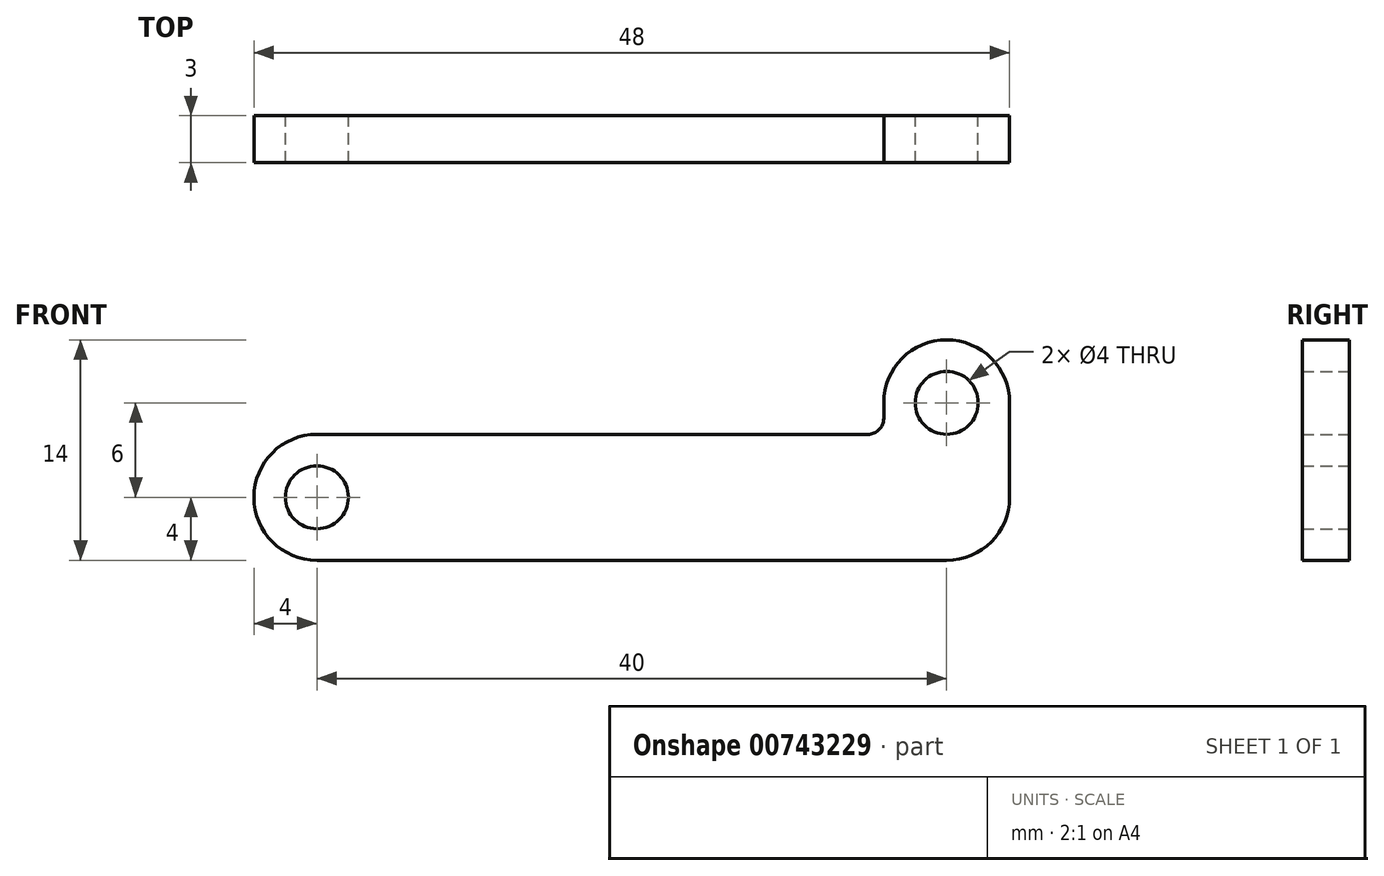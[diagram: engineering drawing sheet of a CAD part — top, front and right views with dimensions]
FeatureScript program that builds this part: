
annotation { "Feature Type Name" : "Feature", "Feature Type Description" : "" }
export const myFeature = defineFeature(function(context is Context, id is Id, definition is map)
    precondition{}
    {
        {
            var Q0;
            Q0=qCreatedBy(makeId("Front.planeOp"),FACE);
            var sketch = newSketch(context, id + "F0", { "sketchPlane" : qUnion([Q0])});
            skLineSegment(sketch, "E0.bottom", {"start": v(-40, 4) * mm, "end": v(-5, 4) * mm});
            skLineSegment(sketch, "E0.top", {"start": v(-40, -4) * mm, "end": v(4, -4) * mm});
            skLineSegment(sketch, "E0.left", {"start": v(-40, 4) * mm, "end": v(-40, -4) * mm, "construction": true});
            skLineSegment(sketch, "E1.bottom", {"start": v(0, -4) * mm, "end": v(-4, -4) * mm});
            skLineSegment(sketch, "E1.top", {"start": v(4, 6) * mm, "end": v(-4, 6) * mm, "construction": true});
            skLineSegment(sketch, "E1.left", {"start": v(4, 4) * mm, "end": v(4, 6) * mm});
            skLineSegment(sketch, "E1.right", {"start": v(-4, 5) * mm, "end": v(-4, 6) * mm});
            skLineSegment(sketch, "E2", {"start": v(4, 4) * mm, "end": v(4, 0) * mm});
            skArc(sketch, "E3", {"start": v(4, 6) * mm, "mid": v(0, 10) * mm, "end": v(-4, 6) * mm});
            skArc(sketch, "E4", {"start": v(-40, 4) * mm, "mid": v(-44, 0) * mm, "end": v(-40, -4) * mm});
            skPoint(sketch, "E5.visualSharp", {"position": v(-4, 4) * mm});
            skArc(sketch, "E5.filletArc", {"start": v(-5, 4) * mm, "mid": v(-4.3, 4.3) * mm, "end": v(-4, 5) * mm});
            skPoint(sketch, "E6.visualSharp", {"position": v(4, -4) * mm});
            skArc(sketch, "E6.filletArc", {"start": v(0, -4) * mm, "mid": v(2.83, -2.83) * mm, "end": v(4, 0) * mm});
            skCircle(sketch, "E7", {"center": v(0, 6) * mm, "radius": 2 * mm});
            skCircle(sketch, "E8", {"center": v(-40, 0) * mm, "radius": 2 * mm});
            skSolve(sketch);
        }
        {
            var Q0;
            Q0=qSketchRegion(id+"F0",true);
            extrude(context, id + "F1", {"entities" : qUnion([Q0]), "depth" : 3 * mm, "offsetDistance" : 25 * mm});
        }
    });
